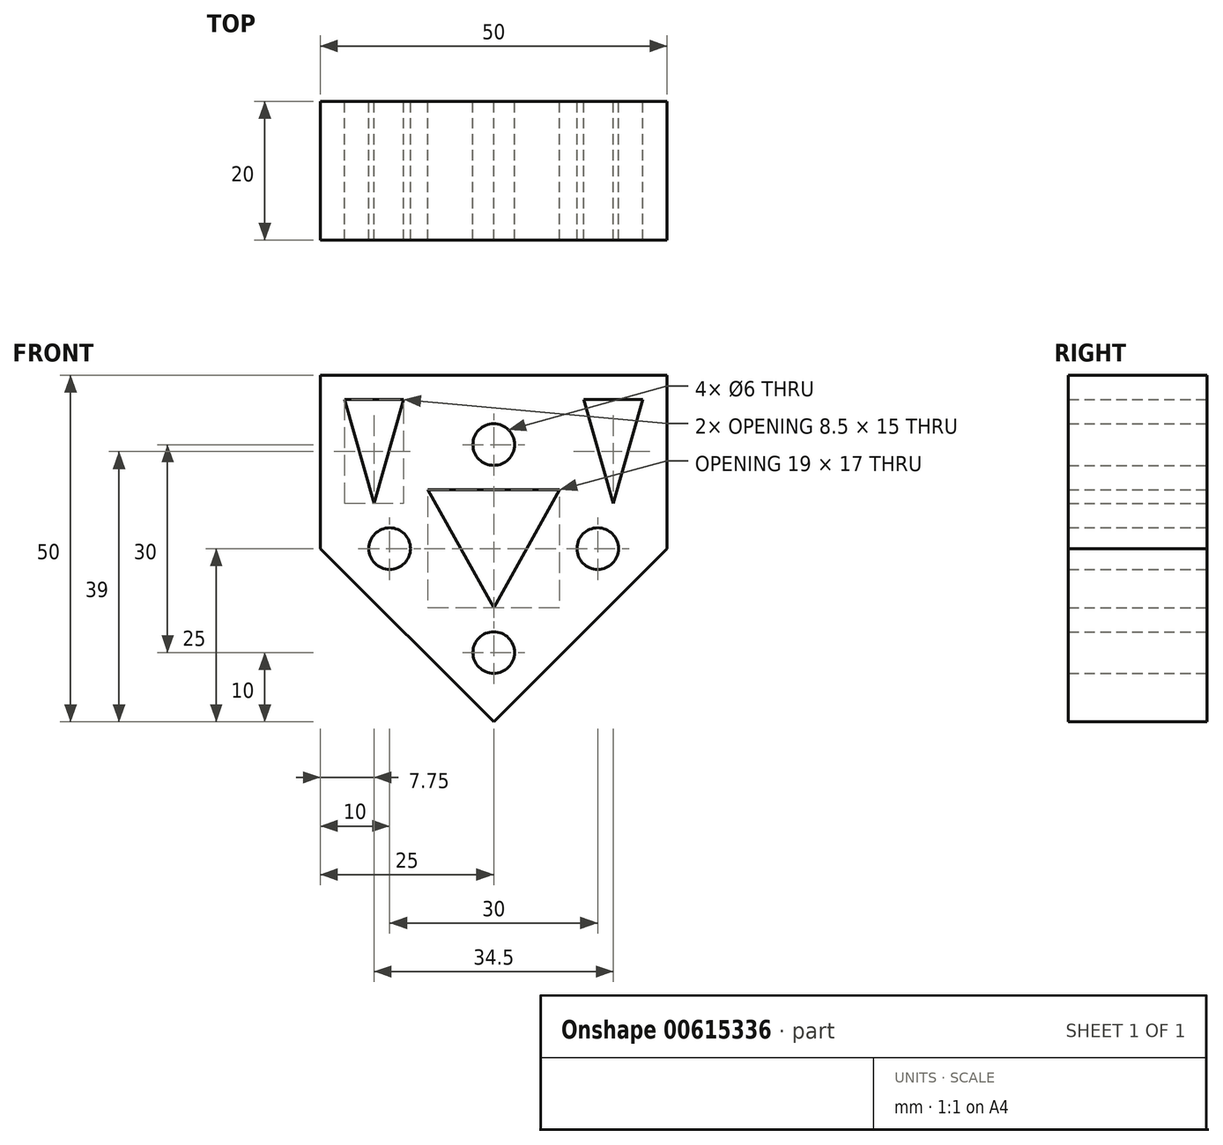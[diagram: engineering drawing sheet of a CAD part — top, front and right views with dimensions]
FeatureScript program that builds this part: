
annotation { "Feature Type Name" : "Feature", "Feature Type Description" : "" }
export const myFeature = defineFeature(function(context is Context, id is Id, definition is map)
    precondition{}
    {
        {
            var Q0;
            Q0=qCreatedBy(makeId("Front.planeOp"),FACE);
            var sketch = newSketch(context, id + "F0", { "sketchPlane" : qUnion([Q0])});
            skLineSegment(sketch, "E0.bottom", {"start": v(25, 25) * mm, "end": v(-25, 25) * mm});
            skLineSegment(sketch, "E0.top", {"start": v(25, -25) * mm, "end": v(-25, -25) * mm});
            skLineSegment(sketch, "E0.left", {"start": v(25, 25) * mm, "end": v(25, -25) * mm});
            skLineSegment(sketch, "E0.right", {"start": v(-25, 25) * mm, "end": v(-25, -25) * mm});
            skPoint(sketch, "E0.middle", {"position": v(0, 0) * mm});
            skLineSegment(sketch, "E1.bottom", {"start": v(15, 15) * mm, "end": v(-15, 15) * mm, "construction": true});
            skLineSegment(sketch, "E1.top", {"start": v(15, -15) * mm, "end": v(-15, -15) * mm, "construction": true});
            skLineSegment(sketch, "E1.left", {"start": v(15, 15) * mm, "end": v(15, -15) * mm, "construction": true});
            skLineSegment(sketch, "E1.right", {"start": v(-15, 15) * mm, "end": v(-15, -15) * mm, "construction": true});
            skLineSegment(sketch, "E2", {"start": v(0, 15) * mm, "end": v(-15, 0) * mm, "construction": true});
            skLineSegment(sketch, "E3", {"start": v(-15, 0) * mm, "end": v(0, -15) * mm, "construction": true});
            skLineSegment(sketch, "E4", {"start": v(0, -15) * mm, "end": v(15, 0) * mm, "construction": true});
            skLineSegment(sketch, "E5", {"start": v(15, 0) * mm, "end": v(0, 15) * mm, "construction": true});
            skCircle(sketch, "E6", {"center": v(0, 15) * mm, "radius": 3 * mm});
            skCircle(sketch, "E7", {"center": v(-15, 0) * mm, "radius": 3 * mm});
            skCircle(sketch, "E8", {"center": v(0, -15) * mm, "radius": 3 * mm});
            skCircle(sketch, "E9", {"center": v(15, 0) * mm, "radius": 3 * mm});
            skLineSegment(sketch, "E10", {"start": v(-19.24, 0) * mm, "end": v(0, 19.24) * mm, "construction": true});
            skLineSegment(sketch, "E11", {"start": v(0, 19.24) * mm, "end": v(19.24, 0) * mm, "construction": true});
            skLineSegment(sketch, "E12", {"start": v(19.24, 0) * mm, "end": v(0, -19.24) * mm, "construction": true});
            skLineSegment(sketch, "E13", {"start": v(0, -19.24) * mm, "end": v(-19.24, 0) * mm, "construction": true});
            skSolve(sketch);
        }
        {
            var Q0;
            Q0=makeQuery(id+"F0.imprint","IMPRINT",FACE,{"disambiguationData":[TD([[makeQuery(id+"F0.imprint","IMPRINT",EDGE,{"derivedFrom":sQuery(id+"F0.wireOp",EDGE,"E0.bottom")}),1.0]])]});
            extrude(context, id + "F1", {"entities" : qUnion([Q0]), "depth" : 20 * mm, "offsetDistance" : 25 * mm});
        }
        {
            var Q0;
            Q0=makeQuery(id+"F1.opExtrude","CAP_FACE",FACE,{"disambiguationData":[OSD([sQuery(id+"F0.wireOp",EDGE,"E0.bottom"),sQuery(id+"F0.wireOp",EDGE,"E0.top"),sQuery(id+"F0.wireOp",EDGE,"E0.left"),sQuery(id+"F0.wireOp",EDGE,"E0.right"),sQuery(id+"F0.wireOp",EDGE,"E6"),sQuery(id+"F0.wireOp",EDGE,"E7"),sQuery(id+"F0.wireOp",EDGE,"E8"),sQuery(id+"F0.wireOp",EDGE,"E9")])],"isStart":true});
            var sketch = newSketch(context, id + "F2", { "sketchPlane" : qUnion([Q0])});
            skLineSegment(sketch, "E14", {"start": v(0, -25) * mm, "end": v(25, 0) * mm});
            skLineSegment(sketch, "E15", {"start": v(0, -25) * mm, "end": v(-25, 0) * mm});
            skLineSegment(sketch, "E16.bottom", {"start": v(9.5, 8.5) * mm, "end": v(-9.5, 8.5) * mm});
            skLineSegment(sketch, "E16.top", {"start": v(9.5, -8.5) * mm, "end": v(-9.5, -8.5) * mm, "construction": true});
            skLineSegment(sketch, "E16.left", {"start": v(9.5, 8.5) * mm, "end": v(9.5, -8.5) * mm, "construction": true});
            skLineSegment(sketch, "E16.right", {"start": v(-9.5, 8.5) * mm, "end": v(-9.5, -8.5) * mm, "construction": true});
            skPoint(sketch, "E16.middle", {"position": v(0, 0) * mm});
            skLineSegment(sketch, "E17", {"start": v(25, 15) * mm, "end": v(-25, 15) * mm, "construction": true});
            skLineSegment(sketch, "E18.bottom", {"start": v(-21.5, 21.5) * mm, "end": v(-13, 21.5) * mm});
            skLineSegment(sketch, "E18.top", {"start": v(-21.5, 6.5) * mm, "end": v(-13, 6.5) * mm, "construction": true});
            skLineSegment(sketch, "E18.left", {"start": v(-21.5, 21.5) * mm, "end": v(-21.5, 6.5) * mm, "construction": true});
            skLineSegment(sketch, "E18.right", {"start": v(-13, 21.5) * mm, "end": v(-13, 6.5) * mm, "construction": true});
            skLineSegment(sketch, "E19.bottom", {"start": v(13, 21.5) * mm, "end": v(21.5, 21.5) * mm});
            skLineSegment(sketch, "E19.top", {"start": v(13, 6.5) * mm, "end": v(21.5, 6.5) * mm, "construction": true});
            skLineSegment(sketch, "E19.left", {"start": v(13, 21.5) * mm, "end": v(13, 6.5) * mm, "construction": true});
            skLineSegment(sketch, "E19.right", {"start": v(21.5, 21.5) * mm, "end": v(21.5, 6.5) * mm, "construction": true});
            skLineSegment(sketch, "E20", {"start": v(-9.5, 8.5) * mm, "end": v(0, -8.5) * mm});
            skLineSegment(sketch, "E21", {"start": v(0, -8.5) * mm, "end": v(9.5, 8.5) * mm});
            skLineSegment(sketch, "E22", {"start": v(13, 21.5) * mm, "end": v(17.25, 6.5) * mm});
            skLineSegment(sketch, "E23", {"start": v(17.25, 6.5) * mm, "end": v(21.5, 21.5) * mm});
            skLineSegment(sketch, "E24", {"start": v(-21.5, 21.5) * mm, "end": v(-17.25, 6.5) * mm});
            skLineSegment(sketch, "E25", {"start": v(-17.25, 6.5) * mm, "end": v(-13, 21.5) * mm});
            skSolve(sketch);
        }
        {
            var Q0;
            Q0=makeQuery(id+"F2.imprint","IMPRINT",FACE,{"disambiguationData":[TD([[makeQuery(id+"F2.imprint","IMPRINT",EDGE,{"derivedFrom":sQuery(id+"F2.wireOp",EDGE,"E18.bottom")}),-1.0]])]});
            var Q1;
            Q1=makeQuery(id+"F2.imprint","IMPRINT",FACE,{"disambiguationData":[TD([[makeQuery(id+"F2.imprint","IMPRINT",EDGE,{"derivedFrom":sQuery(id+"F2.wireOp",EDGE,"E16.bottom")}),1.0]])]});
            var Q2;
            Q2=makeQuery(id+"F2.imprint","IMPRINT",FACE,{"disambiguationData":[TD([[makeQuery(id+"F2.imprint","IMPRINT",EDGE,{"derivedFrom":sQuery(id+"F2.wireOp",EDGE,"E19.bottom")}),-1.0]])]});
            var Q3;
            {var subQ0=sQuery(id+"F2.wireOp",EDGE,"E15");Q3=makeQuery(id+"F2.imprint","IMPRINT",FACE,{"disambiguationData":[TD([[makeQuery(id+"F2.imprint","IMPRINT",EDGE,{"derivedFrom":subQ0}),1.0]])]});}
            var Q4;
            {var subQ0=sQuery(id+"F2.wireOp",EDGE,"E14");Q4=makeQuery(id+"F2.imprint","IMPRINT",FACE,{"disambiguationData":[TD([[makeQuery(id+"F2.imprint","IMPRINT",EDGE,{"derivedFrom":subQ0}),-1.0]])]});}
            extrude(context, id + "F3", {"entities" : qUnion([Q0, Q1, Q2, Q3, Q4]), "operationType" : NewBodyOperationType.REMOVE, "endBound" : BoundingType.THROUGH_ALL, "oppositeDirection" : true, "depth" : 25 * mm, "offsetDistance" : 25 * mm});
        }
    });
